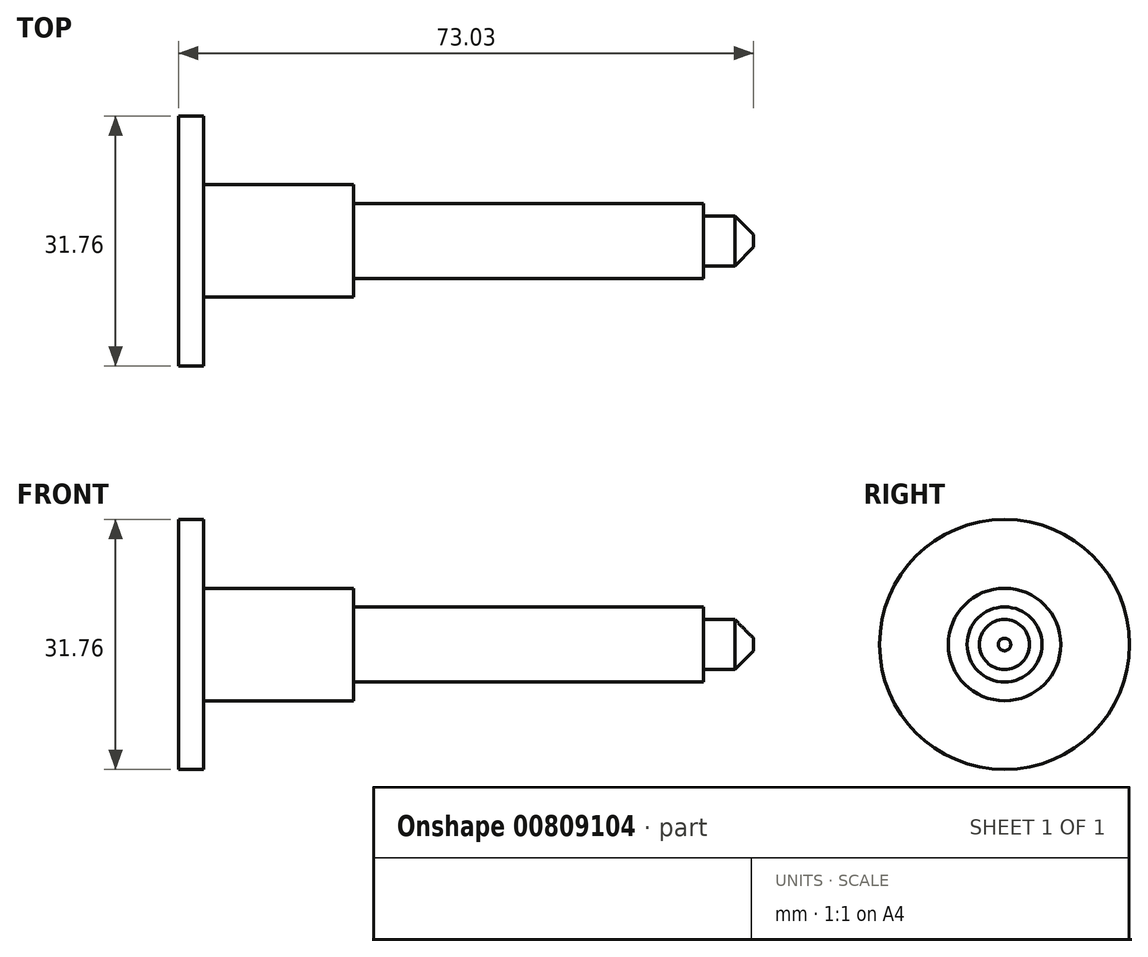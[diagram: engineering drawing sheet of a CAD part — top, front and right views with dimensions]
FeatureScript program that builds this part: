
annotation { "Feature Type Name" : "Feature", "Feature Type Description" : "" }
export const myFeature = defineFeature(function(context is Context, id is Id, definition is map)
    precondition{}
    {
        {
            var Q0;
            Q0=qCreatedBy(makeId("Top.planeOp"),FACE);
            var sketch = newSketch(context, id + "F0", { "sketchPlane" : qUnion([Q0])});
            skLineSegment(sketch, "E0.bottom", {"start": v(0, 0) * mm, "end": v(73.03, 0) * mm});
            skLineSegment(sketch, "E0.top", {"start": v(0, 15.88) * mm, "end": v(73.03, 15.88) * mm});
            skLineSegment(sketch, "E0.left", {"start": v(0, 0) * mm, "end": v(0, 15.88) * mm});
            skLineSegment(sketch, "E0.right", {"start": v(73.03, 0) * mm, "end": v(73.03, 15.88) * mm});
            skLineSegment(sketch, "E1.bottom", {"start": v(3.17, 15.88) * mm, "end": v(131.55, 15.88) * mm});
            skLineSegment(sketch, "E1.top", {"start": v(3.17, 7.14) * mm, "end": v(131.55, 7.14) * mm});
            skLineSegment(sketch, "E1.left", {"start": v(3.17, 15.87) * mm, "end": v(3.17, 7.14) * mm});
            skLineSegment(sketch, "E1.right", {"start": v(131.55, 15.88) * mm, "end": v(131.55, 7.14) * mm});
            skLineSegment(sketch, "E2.bottom", {"start": v(22.23, 7.14) * mm, "end": v(161.38, 7.14) * mm});
            skLineSegment(sketch, "E2.top", {"start": v(22.22, 4.76) * mm, "end": v(161.38, 4.76) * mm});
            skLineSegment(sketch, "E2.left", {"start": v(22.23, 7.14) * mm, "end": v(22.23, 4.76) * mm});
            skLineSegment(sketch, "E2.right", {"start": v(161.38, 7.14) * mm, "end": v(161.38, 4.76) * mm});
            skLineSegment(sketch, "E3.bottom", {"start": v(66.68, 4.76) * mm, "end": v(84.08, 4.76) * mm});
            skLineSegment(sketch, "E3.top", {"start": v(66.68, 3.17) * mm, "end": v(84.08, 3.18) * mm});
            skLineSegment(sketch, "E3.left", {"start": v(66.68, 4.76) * mm, "end": v(66.68, 3.17) * mm});
            skLineSegment(sketch, "E3.right", {"start": v(84.08, 4.76) * mm, "end": v(84.08, 3.18) * mm});
            skSolve(sketch);
        }
        {
            var Q0;
            {var subQ1=sQuery(id+"F0.wireOp",EDGE,"E0.bottom");Q0=makeQuery(id+"F0.imprint","IMPRINT",FACE,{"disambiguationData":[TD([[makeQuery(id+"F0.imprint","IMPRINT",EDGE,{"derivedFrom":subQ1}),1.0]])]});}
            var Q1;
            Q1=sQuery(id+"F0.wireOp",EDGE,"E0.bottom");
            revolve(context, id + "F1", {"surfaceOperationType" : NewSurfaceOperationType.NEW, "entities" : qUnion([Q0]), "axis" : qUnion([Q1]), "revolveType" : RevolveType.FULL});
        }
        {
            var Q0;
            Q0=makeQuery(id+"F1.opRevolve","SWEPT_EDGE",EDGE,{"disambiguationData":[OSD([sQuery(id+"F0.wireOp",EDGE,"E0.right"),sQuery(id+"F0.wireOp",EDGE,"E3.top")])]});
            chamfer(context, id + "F2", {"entities" : qUnion([Q0]), "chamferType" : ChamferType.OFFSET_ANGLE, "width" : 2.38 * mm, "oppositeDirection" : false, "angle" : 45 * degree, "tangentPropagation" : true});
        }
    });
